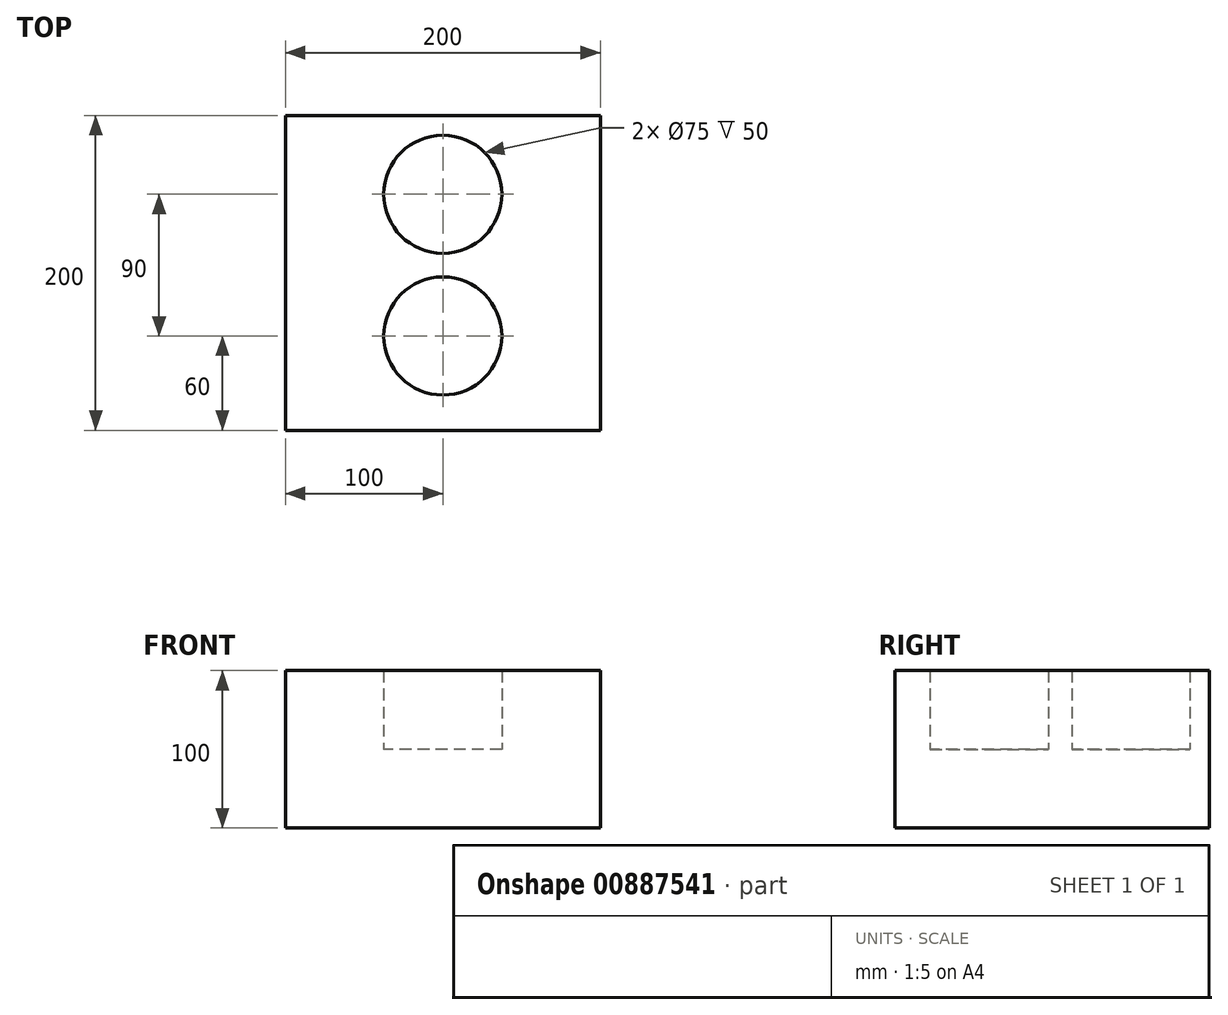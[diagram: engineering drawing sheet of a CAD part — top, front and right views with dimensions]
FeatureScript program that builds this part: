
annotation { "Feature Type Name" : "Feature", "Feature Type Description" : "" }
export const myFeature = defineFeature(function(context is Context, id is Id, definition is map)
    precondition{}
    {
        {
            assignVariable(context, id + "F0", {"name" : "Height", "anyValue" : 100});
        }
        {
            assignVariable(context, id + "F1", {"name" : "CupHeight", "anyValue" : 50});
        }
        {
            var Q0;
            Q0=qCreatedBy(makeId("Top.planeOp"),FACE);
            var sketch = newSketch(context, id + "F2", { "sketchPlane" : qUnion([Q0])});
            skLineSegment(sketch, "E0.bottom", {"start": v(100, -100) * mm, "end": v(-100, -100) * mm});
            skLineSegment(sketch, "E0.top", {"start": v(100, 100) * mm, "end": v(-100, 100) * mm});
            skLineSegment(sketch, "E0.left", {"start": v(100, -100) * mm, "end": v(100, 100) * mm});
            skLineSegment(sketch, "E0.right", {"start": v(-100, -100) * mm, "end": v(-100, 100) * mm});
            skPoint(sketch, "E0.middle", {"position": v(0, 0) * mm});
            skLineSegment(sketch, "E1", {"start": v(0, 100) * mm, "end": v(0, -100) * mm, "construction": true});
            skCircle(sketch, "E2", {"center": v(0, 50) * mm, "radius": 37.5 * mm});
            skCircle(sketch, "E3", {"center": v(0, -40) * mm, "radius": 37.5 * mm});
            skSolve(sketch);
        }
        {
            var Q0;
            Q0=makeQuery(id+"F2.imprint","IMPRINT",FACE,{"disambiguationData":[TD([[makeQuery(id+"F2.imprint","IMPRINT",EDGE,{"derivedFrom":sQuery(id+"F2.wireOp",EDGE,"E0.bottom")}),-1.0]])]});
            var Q1;
            Q1=makeQuery(id+"F2.imprint","IMPRINT",FACE,{"disambiguationData":[TD([[makeQuery(id+"F2.imprint","IMPRINT",EDGE,{"derivedFrom":sQuery(id+"F2.wireOp",EDGE,"E3")}),1.0]])]});
            var Q2;
            Q2=makeQuery(id+"F2.imprint","IMPRINT",FACE,{"disambiguationData":[TD([[makeQuery(id+"F2.imprint","IMPRINT",EDGE,{"derivedFrom":sQuery(id+"F2.wireOp",EDGE,"E2")}),1.0]])]});
            extrude(context, id + "F3", {"entities" : qUnion([Q0, Q1, Q2]), "oppositeDirection" : true, "depth" : (getVariable(context, 'Height') - getVariable(context, 'CupHeight')) * mm, "offsetDistance" : 25 * mm});
        }
        {
            var Q0;
            Q0=makeQuery(id+"F2.imprint","IMPRINT",FACE,{"disambiguationData":[TD([[makeQuery(id+"F2.imprint","IMPRINT",EDGE,{"derivedFrom":sQuery(id+"F2.wireOp",EDGE,"E0.bottom")}),-1.0]])]});
            extrude(context, id + "F4", {"entities" : qUnion([Q0]), "operationType" : NewBodyOperationType.ADD, "depth" : (getVariable(context, 'CupHeight')) * mm, "offsetDistance" : 25 * mm});
        }
    });
